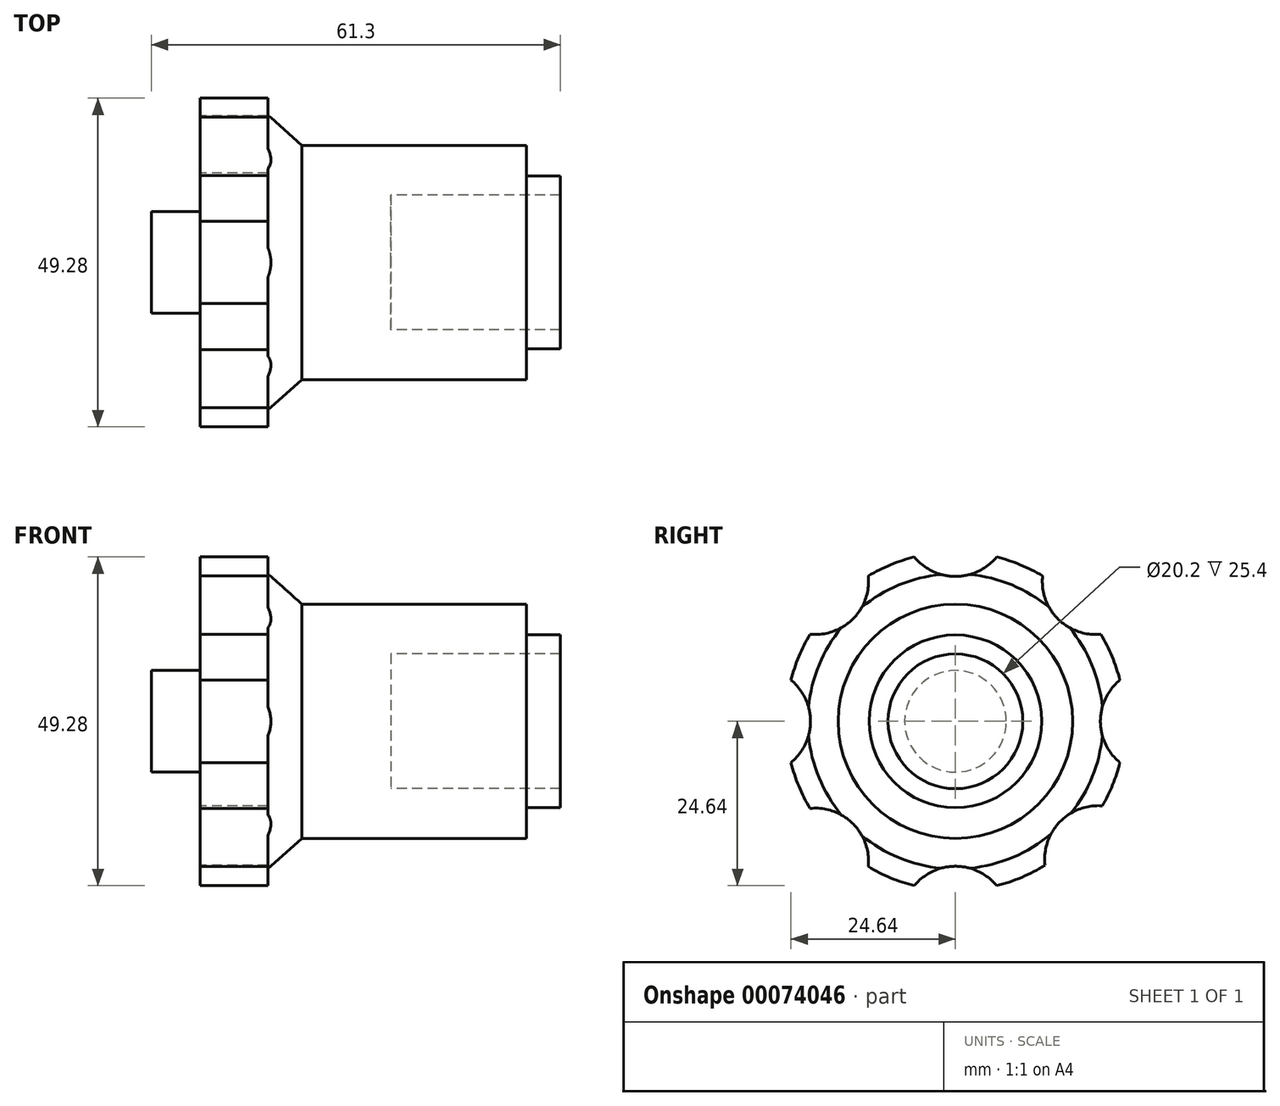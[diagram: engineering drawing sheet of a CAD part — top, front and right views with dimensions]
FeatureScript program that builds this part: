
annotation { "Feature Type Name" : "Feature", "Feature Type Description" : "" }
export const myFeature = defineFeature(function(context is Context, id is Id, definition is map)
    precondition{}
    {
        {
            var Q0;
            Q0=qCreatedBy(makeId("Front.planeOp"),FACE);
            var sketch = newSketch(context, id + "F0", { "sketchPlane" : qUnion([Q0])});
            skLineSegment(sketch, "E0", {"start": v(24.93, 12.54) * mm, "end": v(24.93, 7.92) * mm});
            skLineSegment(sketch, "E1.0", {"start": v(30, 7.92) * mm, "end": v(30, 5.08) * mm});
            skLineSegment(sketch, "E2", {"start": v(24.93, 7.92) * mm, "end": v(30, 7.92) * mm});
            skLineSegment(sketch, "E3", {"start": v(-8.73, 12.54) * mm, "end": v(24.93, 12.54) * mm});
            skLineSegment(sketch, "E4", {"start": v(-13.8, 17.1) * mm, "end": v(-8.73, 12.54) * mm});
            skLineSegment(sketch, "E5.0", {"start": v(4.6, 5.08) * mm, "end": v(4.6, -5.02) * mm});
            skLineSegment(sketch, "E6", {"start": v(30, 5.08) * mm, "end": v(4.6, 5.08) * mm});
            skLineSegment(sketch, "E7", {"start": v(-31.3, -5.02) * mm, "end": v(4.6, -5.02) * mm});
            skLineSegment(sketch, "E8.0", {"start": v(-23.97, 20.38) * mm, "end": v(-13.8, 20.38) * mm});
            skLineSegment(sketch, "E9", {"start": v(-13.8, 17.1) * mm, "end": v(-13.8, 20.38) * mm});
            skLineSegment(sketch, "E10.0", {"start": v(-31.3, 2.6) * mm, "end": v(-23.97, 2.6) * mm});
            skLineSegment(sketch, "E11", {"start": v(-31.3, 2.6) * mm, "end": v(-31.3, -5.02) * mm});
            skLineSegment(sketch, "E12", {"start": v(-23.97, 20.38) * mm, "end": v(-23.97, 2.6) * mm});
            skSolve(sketch);
        }
        {
            var Q0;
            Q0=makeQuery(id+"F0.imprint","IMPRINT",FACE,{"disambiguationData":[TD([[makeQuery(id+"F0.imprint","IMPRINT",EDGE,{"derivedFrom":sQuery(id+"F0.wireOp",EDGE,"E0")}),-1.0]])]});
            var Q1;
            Q1=sQuery(id+"F0.wireOp",EDGE,"E7");
            var Q2;
            Q2=sQuery(id+"F0.wireOp",EDGE,"E7");
            revolve(context, id + "F1", {"entities" : qUnion([Q0]), "surfaceEntities" : qUnion([Q1]), "axis" : qUnion([Q2]), "revolveType" : RevolveType.FULL});
        }
        {
            var Q0;
            Q0=makeQuery(id+"F1.opRevolve","SWEPT_FACE",FACE,{"disambiguationData":[OSD([sQuery(id+"F0.wireOp",EDGE,"E12")])]});
            var sketch = newSketch(context, id + "F2", { "sketchPlane" : qUnion([Q0])});
            skCircle(sketch, "E13", {"center": v(0, -5.02) * mm, "radius": 29.72 * mm, "construction": true});
            skLineSegment(sketch, "E14", {"start": v(0, -5.02) * mm, "end": v(0, 24.7) * mm});
            skLineSegment(sketch, "E15", {"start": v(0, -5.02) * mm, "end": v(0, -34.74) * mm});
            skLineSegment(sketch, "E16", {"start": v(0, -5.02) * mm, "end": v(-29.72, -5.02) * mm});
            skLineSegment(sketch, "E17", {"start": v(0, -5.02) * mm, "end": v(29.72, -5.02) * mm});
            skLineSegment(sketch, "E18", {"start": v(0, -5.02) * mm, "end": v(-21.02, 16) * mm});
            skLineSegment(sketch, "E19", {"start": v(0, -5.02) * mm, "end": v(21.02, 16) * mm});
            skLineSegment(sketch, "E20", {"start": v(0, -5.02) * mm, "end": v(21.02, -26.04) * mm});
            skLineSegment(sketch, "E21", {"start": v(0, -5.02) * mm, "end": v(-21.38, -25.67) * mm});
            skCircle(sketch, "E22", {"center": v(-21.02, 16) * mm, "radius": 8 * mm});
            skCircle(sketch, "E23", {"center": v(0, 24.7) * mm, "radius": 8 * mm});
            skCircle(sketch, "E24", {"center": v(21.02, 16) * mm, "radius": 8 * mm});
            skCircle(sketch, "E25", {"center": v(29.72, -5.02) * mm, "radius": 8 * mm});
            skCircle(sketch, "E26", {"center": v(21.02, -26.04) * mm, "radius": 8 * mm});
            skCircle(sketch, "E27", {"center": v(0, -34.74) * mm, "radius": 8 * mm});
            skCircle(sketch, "E28", {"center": v(-21.38, -25.67) * mm, "radius": 8 * mm});
            skCircle(sketch, "E29", {"center": v(-29.72, -5.02) * mm, "radius": 8 * mm});
            skSolve(sketch);
        }
        {
            var Q0;
            Q0 = qSketchRegion(id + "F2", true);
            extrude(context, id + "F3", {"entities" : qUnion([Q0]), "operationType" : NewBodyOperationType.REMOVE, "oppositeDirection" : true, "depth" : 25 * mm});
        }
    });
